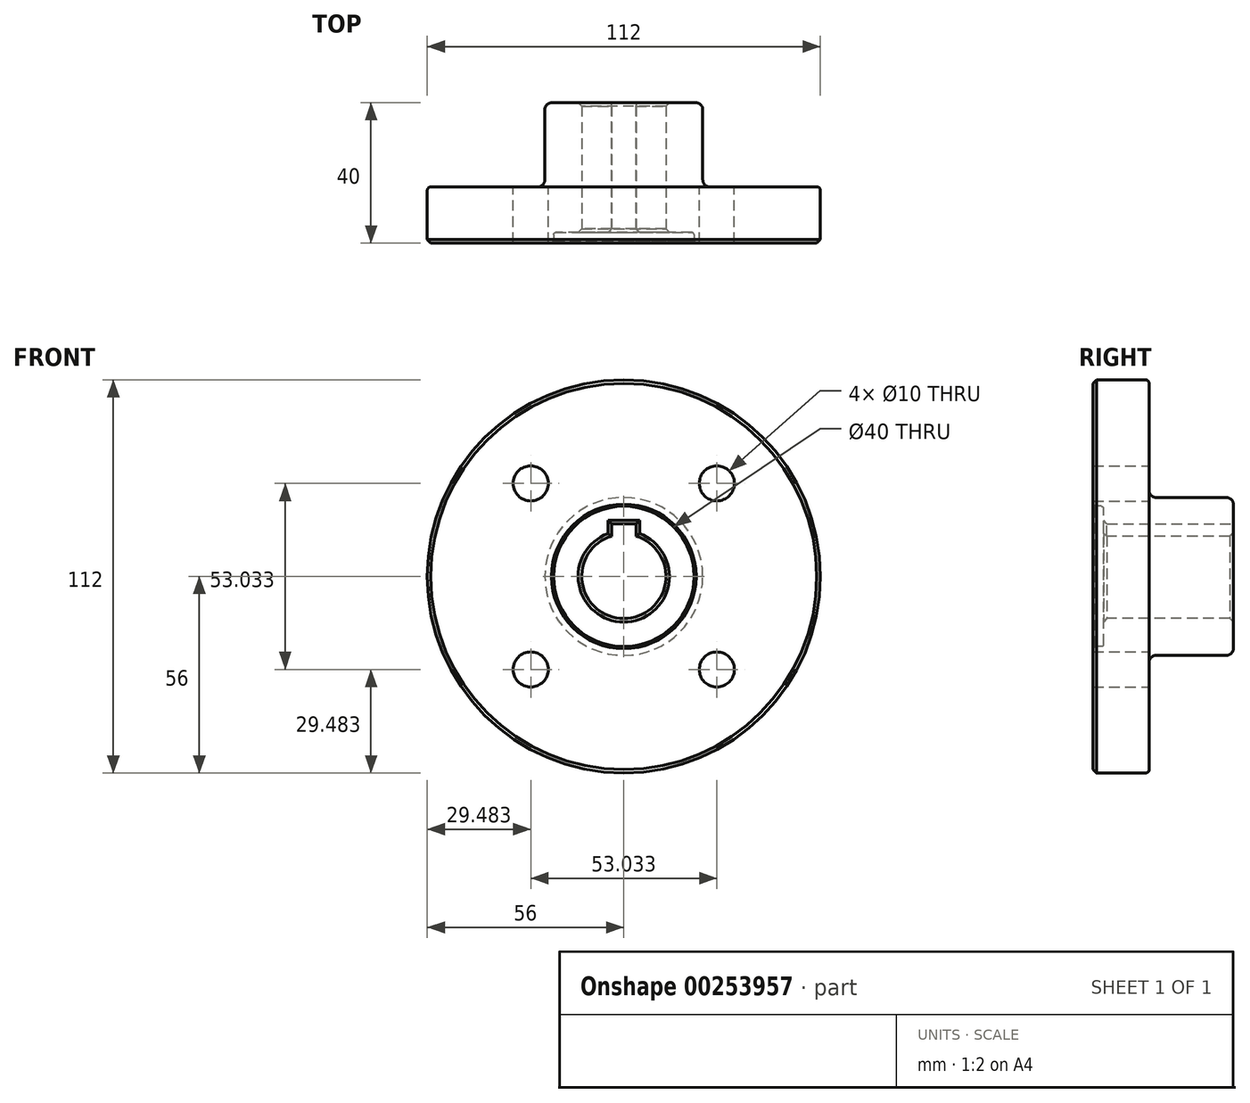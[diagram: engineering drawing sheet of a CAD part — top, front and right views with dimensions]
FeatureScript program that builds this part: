
annotation { "Feature Type Name" : "Feature", "Feature Type Description" : "" }
export const myFeature = defineFeature(function(context is Context, id is Id, definition is map)
    precondition{}
    {
        {
            var Q0;
            Q0=qCreatedBy(makeId("Right.planeOp"),FACE);
            var sketch = newSketch(context, id + "F0", { "sketchPlane" : qUnion([Q0])});
            skLineSegment(sketch, "E0", {"start": v(0, 20) * mm, "end": v(0, 56) * mm});
            skLineSegment(sketch, "E1", {"start": v(0, 56) * mm, "end": v(16, 56) * mm});
            skLineSegment(sketch, "E2", {"start": v(16, 56) * mm, "end": v(16, 22.5) * mm});
            skLineSegment(sketch, "E3", {"start": v(16, 22.5) * mm, "end": v(40, 22.5) * mm});
            skLineSegment(sketch, "E4", {"start": v(40, 22.5) * mm, "end": v(40, 12) * mm});
            skLineSegment(sketch, "E5", {"start": v(40, 12) * mm, "end": v(3, 12) * mm});
            skLineSegment(sketch, "E6", {"start": v(3, 12) * mm, "end": v(3, 20) * mm});
            skLineSegment(sketch, "E7", {"start": v(3, 20) * mm, "end": v(0, 20) * mm});
            skLineSegment(sketch, "E8", {"start": v(-21.93, 0) * mm, "end": v(44.22, 0) * mm, "construction": true});
            skSolve(sketch);
        }
        {
            var Q0;
            Q0=makeQuery(id+"F0.imprint","IMPRINT",FACE,{"disambiguationData":[TD([[makeQuery(id+"F0.imprint","IMPRINT",EDGE,{"derivedFrom":sQuery(id+"F0.wireOp",EDGE,"E0")}),-1.0]])]});
            var Q1;
            Q1=sQuery(id+"F0.wireOp",EDGE,"E8");
            revolve(context, id + "F1", {"entities" : qUnion([Q0]), "axis" : qUnion([Q1]), "revolveType" : RevolveType.FULL});
        }
        {
            var Q0;
            Q0=makeQuery(id+"F1.opRevolve","SWEPT_FACE",FACE,{"disambiguationData":[OSD([sQuery(id+"F0.wireOp",EDGE,"E4")])]});
            var sketch = newSketch(context, id + "F2", { "sketchPlane" : qUnion([Q0])});
            skLineSegment(sketch, "E9.bottom", {"start": v(-3.5, 15) * mm, "end": v(3.5, 15) * mm});
            skLineSegment(sketch, "E9.top", {"start": v(-3.5, 8) * mm, "end": v(3.5, 8) * mm});
            skLineSegment(sketch, "E9.left", {"start": v(-3.5, 15) * mm, "end": v(-3.5, 8) * mm});
            skLineSegment(sketch, "E9.right", {"start": v(3.5, 15) * mm, "end": v(3.5, 8) * mm});
            skSolve(sketch);
        }
        {
            var Q0;
            Q0 = qSketchRegion(id + "F2", true);
            extrude(context, id + "F3", {"entities" : qUnion([Q0]), "operationType" : NewBodyOperationType.REMOVE, "endBound" : BoundingType.THROUGH_ALL, "oppositeDirection" : true, "depth" : 25 * mm});
        }
        {
            var Q0;
            Q0=makeQuery(id+"F1.opRevolve","SWEPT_FACE",FACE,{"disambiguationData":[OSD([sQuery(id+"F0.wireOp",EDGE,"E2")])]});
            var sketch = newSketch(context, id + "F4", { "sketchPlane" : qUnion([Q0])});
            skCircle(sketch, "E10", {"center": v(0, 0) * mm, "radius": 37.5 * mm, "construction": true});
            skLineSegment(sketch, "E11", {"start": v(0, 0) * mm, "end": v(31.93, 31.93) * mm, "construction": true});
            skPoint(sketch, "E12", {"position": v(26.52, 26.52) * mm});
            skPoint(sketch, "E13.1.0", {"position": v(-26.52, 26.52) * mm});
            skPoint(sketch, "E13.2.0", {"position": v(-26.52, -26.52) * mm});
            skPoint(sketch, "E13.3.0", {"position": v(26.52, -26.52) * mm});
            skSolve(sketch);
        }
        {
            var Q0;
            Q0=sQuery(id+"F4.wireOp",VERTEX,"E12");
            var Q1;
            Q1=sQuery(id+"F4.wireOp",VERTEX,"E13.1.0");
            var Q2;
            Q2=sQuery(id+"F4.wireOp",VERTEX,"E13.2.0");
            var Q3;
            Q3=sQuery(id+"F4.wireOp",VERTEX,"E13.3.0");
            var Q4;
            Q4=makeQuery(id+"F1.opRevolve","SWEPT_BODY",BODY,{"disambiguationData":[OSD([sQuery(id+"F0.wireOp",EDGE,"E0"),sQuery(id+"F0.wireOp",EDGE,"E1"),sQuery(id+"F0.wireOp",EDGE,"E2"),sQuery(id+"F0.wireOp",EDGE,"E3"),sQuery(id+"F0.wireOp",EDGE,"E4"),sQuery(id+"F0.wireOp",EDGE,"E5"),sQuery(id+"F0.wireOp",EDGE,"E6"),sQuery(id+"F0.wireOp",EDGE,"E7")])]});
            hole(context, id + "F5", {"style" : HoleStyle.SIMPLE, "endStyle" : HoleEndStyle.THROUGH, "holeDiameter" : 10 * mm, "tappedDepth" : 12 * mm, "tapClearance" : 3, "locations" : qUnion([Q0, Q1, Q2, Q3]), "scope" : qUnion([Q4])});
        }
        {
            var Q0;
            Q0=makeQuery(id+"F1.opRevolve","SWEPT_EDGE",EDGE,{"disambiguationData":[OSD([sQuery(id+"F0.wireOp",EDGE,"E5"),sQuery(id+"F0.wireOp",EDGE,"E6")])]});
            var Q1;
            Q1=makeQuery(id+"F3.boolean.opBoolean","COPY",EDGE,{"derivedFrom":makeQuery(id+"F3.opExtrude","CAP_EDGE",EDGE,{"disambiguationData":[OSD([sQuery(id+"F2.wireOp",EDGE,"E9.right")])],"isStart":true})});
            var Q2;
            Q2=makeQuery(id+"F3.boolean.opBoolean","COPY",EDGE,{"derivedFrom":makeQuery(id+"F3.opExtrude","CAP_EDGE",EDGE,{"disambiguationData":[OSD([sQuery(id+"F2.wireOp",EDGE,"E9.bottom")])],"isStart":true})});
            var Q3;
            Q3=makeQuery(id+"F3.boolean.opBoolean","COPY",EDGE,{"derivedFrom":makeQuery(id+"F3.opExtrude","CAP_EDGE",EDGE,{"disambiguationData":[OSD([sQuery(id+"F2.wireOp",EDGE,"E9.left")])],"isStart":true})});
            var Q4;
            Q4=makeQuery(id+"F3.boolean.opBoolean","INTERSECT",EDGE,{"derivedFrom":[makeQuery(id+"F1.opRevolve","SWEPT_FACE",FACE,{"disambiguationData":[OSD([sQuery(id+"F0.wireOp",EDGE,"E6")])]}),makeQuery(id+"F3.opExtrude","SWEPT_FACE",FACE,{"disambiguationData":[OSD([sQuery(id+"F2.wireOp",EDGE,"E9.right")])]})]});
            var Q5;
            Q5=makeQuery(id+"F1.opRevolve","SWEPT_EDGE",EDGE,{"disambiguationData":[OSD([sQuery(id+"F0.wireOp",EDGE,"E4"),sQuery(id+"F0.wireOp",EDGE,"E5")])]});
            var Q6;
            Q6=makeQuery(id+"F3.boolean.opBoolean","INTERSECT",EDGE,{"derivedFrom":[makeQuery(id+"F1.opRevolve","SWEPT_FACE",FACE,{"disambiguationData":[OSD([sQuery(id+"F0.wireOp",EDGE,"E6")])]}),makeQuery(id+"F3.opExtrude","SWEPT_FACE",FACE,{"disambiguationData":[OSD([sQuery(id+"F2.wireOp",EDGE,"E9.left")])]})]});
            var Q7;
            Q7=makeQuery(id+"F3.boolean.opBoolean","INTERSECT",EDGE,{"derivedFrom":[makeQuery(id+"F1.opRevolve","SWEPT_FACE",FACE,{"disambiguationData":[OSD([sQuery(id+"F0.wireOp",EDGE,"E6")])]}),makeQuery(id+"F3.opExtrude","SWEPT_FACE",FACE,{"disambiguationData":[OSD([sQuery(id+"F2.wireOp",EDGE,"E9.bottom")])]})]});
            chamfer(context, id + "F6", {"entities" : qUnion([Q0, Q1, Q2, Q3, Q4, Q5, Q6, Q7]), "width" : 1 * mm, "tangentPropagation" : true});
        }
        {
            var Q0;
            Q0=makeQuery(id+"F1.opRevolve","SWEPT_EDGE",EDGE,{"disambiguationData":[OSD([sQuery(id+"F0.wireOp",EDGE,"E0"),sQuery(id+"F0.wireOp",EDGE,"E7")])]});
            chamfer(context, id + "F7", {"entities" : qUnion([Q0]), "width" : 0.6 * mm, "tangentPropagation" : true});
        }
        {
            var Q0;
            Q0=makeQuery(id+"F1.opRevolve","SWEPT_EDGE",EDGE,{"disambiguationData":[OSD([sQuery(id+"F0.wireOp",EDGE,"E6"),sQuery(id+"F0.wireOp",EDGE,"E7")])]});
            fillet(context, id + "F8", {"entities" : qUnion([Q0]), "radius" : 0.6 * mm, "tangentPropagation" : true, "allowEdgeOverflow" : false});
        }
        {
            var Q0;
            Q0=makeQuery(id+"F1.opRevolve","SWEPT_EDGE",EDGE,{"disambiguationData":[OSD([sQuery(id+"F0.wireOp",EDGE,"E0"),sQuery(id+"F0.wireOp",EDGE,"E1")])]});
            chamfer(context, id + "F9", {"entities" : qUnion([Q0]), "width" : 1 * mm, "tangentPropagation" : true});
        }
        {
            var Q0;
            Q0=makeQuery(id+"F1.opRevolve","SWEPT_EDGE",EDGE,{"disambiguationData":[OSD([sQuery(id+"F0.wireOp",EDGE,"E1"),sQuery(id+"F0.wireOp",EDGE,"E2")])]});
            fillet(context, id + "F10", {"entities" : qUnion([Q0]), "radius" : 1 * mm, "tangentPropagation" : true, "allowEdgeOverflow" : false});
        }
        {
            var Q0;
            Q0=makeQuery(id+"F1.opRevolve","SWEPT_EDGE",EDGE,{"disambiguationData":[OSD([sQuery(id+"F0.wireOp",EDGE,"E3"),sQuery(id+"F0.wireOp",EDGE,"E4")])]});
            var Q1;
            Q1=makeQuery(id+"F1.opRevolve","SWEPT_EDGE",EDGE,{"disambiguationData":[OSD([sQuery(id+"F0.wireOp",EDGE,"E2"),sQuery(id+"F0.wireOp",EDGE,"E3")])]});
            fillet(context, id + "F11", {"entities" : qUnion([Q0, Q1]), "radius" : 2 * mm, "tangentPropagation" : true, "allowEdgeOverflow" : false});
        }
    });
